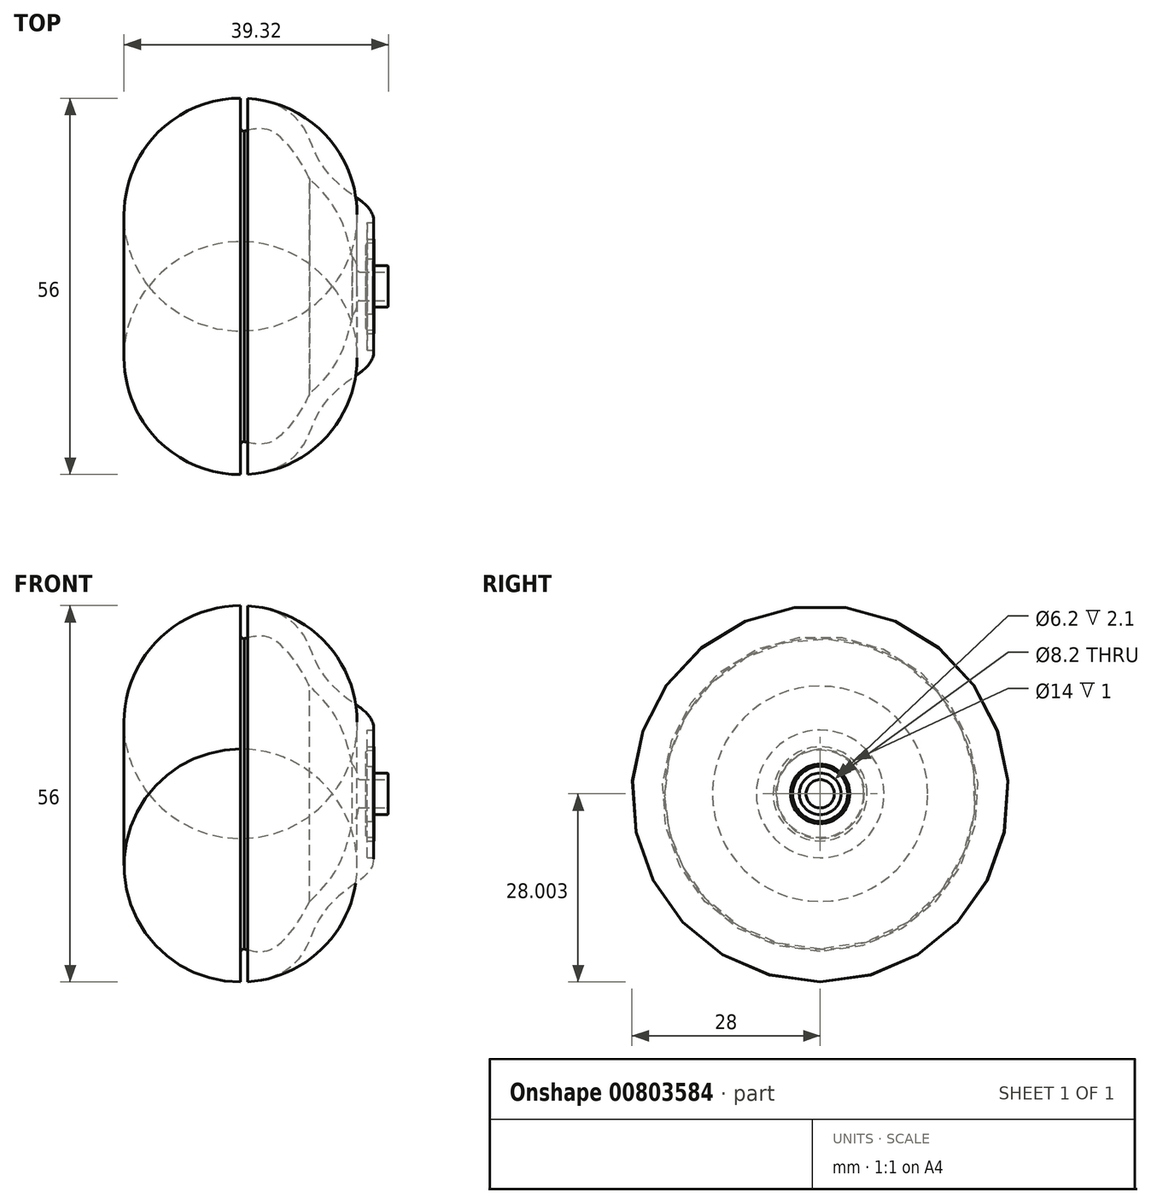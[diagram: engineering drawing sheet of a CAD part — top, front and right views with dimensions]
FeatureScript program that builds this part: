
annotation { "Feature Type Name" : "Feature", "Feature Type Description" : "" }
export const myFeature = defineFeature(function(context is Context, id is Id, definition is map)
    precondition{}
    {
        {
            var Q0;
            Q0=qCreatedBy(makeId("Front.planeOp"),FACE);
            var sketch = newSketch(context, id + "F0", { "sketchPlane" : qUnion([Q0])});
            skPoint(sketch, "E0", {"position": v(100.34, -4.5) * mm});
            skLineSegment(sketch, "E1", {"start": v(103.46, -7.12) * mm, "end": v(103.46, -6.52) * mm});
            skLineSegment(sketch, "E2", {"start": v(103.26, -6.32) * mm, "end": v(101.16, -6.32) * mm});
            skLineSegment(sketch, "E3", {"start": v(101.16, -6.32) * mm, "end": v(101.16, -5.52) * mm});
            skLineSegment(sketch, "E4", {"start": v(100.96, -5.32) * mm, "end": v(100.36, -5.32) * mm});
            skLineSegment(sketch, "E5", {"start": v(100.16, -5.12) * mm, "end": v(100.16, -3.16) * mm});
            skLineSegment(sketch, "E6", {"start": v(100.35, -2.96) * mm, "end": v(101.3, -2.94) * mm});
            skLineSegment(sketch, "E7", {"start": v(101.3, -2.94) * mm, "end": v(101.3, -2.42) * mm});
            skLineSegment(sketch, "E8", {"start": v(101.3, -2.42) * mm, "end": v(100.3, -2.42) * mm});
            skLineSegment(sketch, "E9", {"start": v(100.3, -2.42) * mm, "end": v(100.3, 0.08) * mm});
            skLineSegment(sketch, "E10", {"start": v(100.3, 0.08) * mm, "end": v(101.1, 0.08) * mm});
            skPoint(sketch, "E11.startSnap0", {"position": v(102.3, -6.32) * mm});
            skLineSegment(sketch, "E12", {"start": v(103.46, -9.42) * mm, "end": v(102.18, -9.42) * mm});
            skLineSegment(sketch, "E13", {"start": v(103.46, -9.42) * mm, "end": v(81.46, -9.42) * mm});
            skLineSegment(sketch, "E14", {"start": v(81.46, -9.42) * mm, "end": v(81.46, 18.58) * mm});
            skFitSpline(sketch, "E15", {"points": [v(101.3, 0.08) * mm, v(97.77, 4.46) * mm, v(93.16, 9.24) * mm, v(90.38, 14.84) * mm, v(81.46, 18.58) * mm], "startDerivative": vector(0, 28.99) * mm, "endDerivative": vector(-45.1, 0) * mm});
            skLineSegment(sketch, "E16", {"start": v(81.46, 17.55) * mm, "end": v(81.46, 14.18) * mm});
            skPoint(sketch, "E17.visualSharp", {"position": v(98.76, -7.32) * mm});
            skPoint(sketch, "E18.visualSharp", {"position": v(103.46, -7.32) * mm});
            skArc(sketch, "E18.filletArc", {"start": v(103.26, -7.32) * mm, "mid": v(103.4, -7.26) * mm, "end": v(103.46, -7.12) * mm});
            skPoint(sketch, "E19.visualSharp", {"position": v(103.46, -6.32) * mm});
            skArc(sketch, "E19.filletArc", {"start": v(103.46, -6.52) * mm, "mid": v(103.4, -6.38) * mm, "end": v(103.26, -6.32) * mm});
            skPoint(sketch, "E20.visualSharp", {"position": v(101.16, -5.32) * mm});
            skArc(sketch, "E20.filletArc", {"start": v(101.16, -5.52) * mm, "mid": v(101.1, -5.38) * mm, "end": v(100.96, -5.32) * mm});
            skPoint(sketch, "E21.visualSharp", {"position": v(100.16, -5.32) * mm});
            skArc(sketch, "E21.filletArc", {"start": v(100.16, -5.12) * mm, "mid": v(100.21, -5.26) * mm, "end": v(100.36, -5.32) * mm});
            skPoint(sketch, "E22.visualSharp", {"position": v(100.16, -2.97) * mm});
            skArc(sketch, "E22.filletArc", {"start": v(100.35, -2.96) * mm, "mid": v(100.21, -3.02) * mm, "end": v(100.16, -3.16) * mm});
            skArc(sketch, "E23.filletArc", {"start": v(101.1, 0.08) * mm, "mid": v(101.24, 0.15) * mm, "end": v(101.3, 0.3) * mm});
            skArc(sketch, "E24.filletArc", {"start": v(82.53, 18.55) * mm, "mid": v(81.78, 18.28) * mm, "end": v(81.46, 17.55) * mm});
            skPoint(sketch, "E25.visualSharp", {"position": v(81.46, 13.58) * mm});
            skArc(sketch, "E25.filletArc", {"start": v(81.46, 14.18) * mm, "mid": v(81.64, 13.8) * mm, "end": v(82.04, 13.69) * mm});
            skFitSpline(sketch, "E26", {"points": [v(82.04, 13.69) * mm, v(86.07, 13.69) * mm, v(91.73, 6.6) * mm], "startDerivative": vector(10.13, 2.36) * mm, "endDerivative": vector(6.95, -14.66) * mm});
            skFitSpline(sketch, "E27", {"points": [v(91.73, 6.6) * mm, v(97.12, -1.41) * mm, v(98.46, -7.15) * mm], "startDerivative": vector(18, -16.7) * mm, "endDerivative": vector(0.58, -7.66) * mm});
            skLineSegment(sketch, "E28", {"start": v(103.46, -9.42) * mm, "end": v(98.96, -9.42) * mm});
            skFitSpline(sketch, "E29", {"points": [v(98.96, -7.32) * mm, v(98.76, -6.2) * mm, v(98.1, -5) * mm], "startDerivative": vector(-0.24, 2.34) * mm, "endDerivative": vector(-1.48, 2.3) * mm});
            skLineSegment(sketch, "E30.trimOffspring", {"start": v(99.14, -7.32) * mm, "end": v(103.26, -7.32) * mm});
            skArc(sketch, "E31.filletArc", {"start": v(98.95, -7.14) * mm, "mid": v(99.01, -7.27) * mm, "end": v(99.14, -7.32) * mm});
            skSolve(sketch);
        }
        {
            var Q0;
            Q0 = qSketchRegion(id + "F0", true);
            var Q1;
            Q1=sQuery(id+"F0.wireOp",EDGE,"E13");
            revolve(context, id + "F1", {"surfaceOperationType" : NewSurfaceOperationType.NEW, "entities" : qUnion([Q0]), "axis" : qUnion([Q1]), "revolveType" : RevolveType.FULL});
        }
    });
